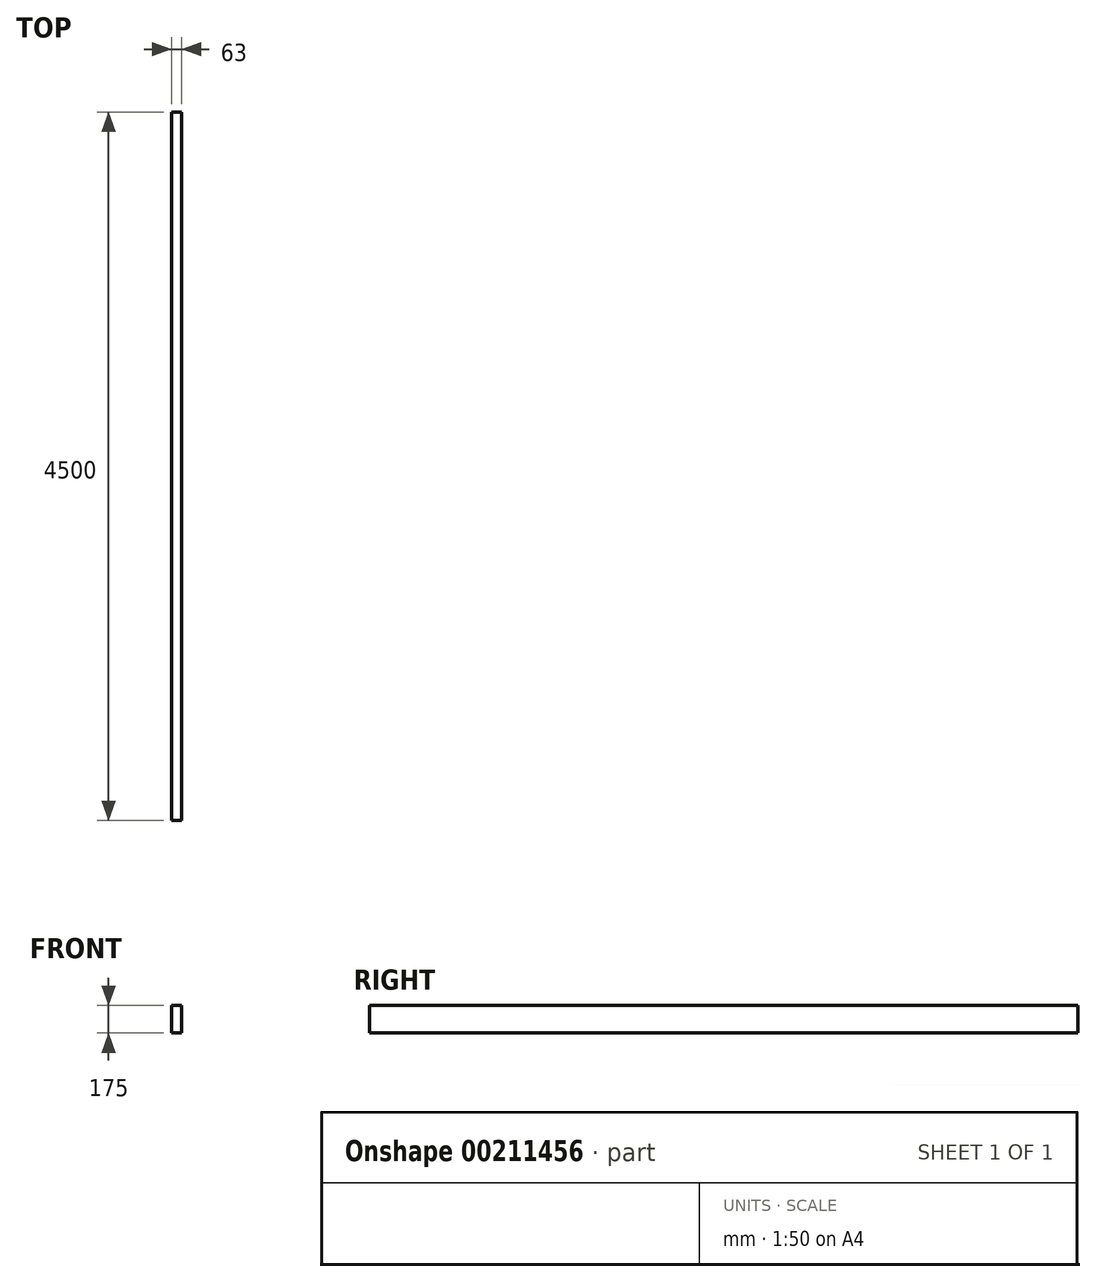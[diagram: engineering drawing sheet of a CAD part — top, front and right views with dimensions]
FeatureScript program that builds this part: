
annotation { "Feature Type Name" : "Feature", "Feature Type Description" : "" }
export const myFeature = defineFeature(function(context is Context, id is Id, definition is map)
    precondition{}
    {
        {
            var Q0;
            Q0=qCreatedBy(makeId("Front.planeOp"),FACE);
            var sketch = newSketch(context, id + "F0", { "sketchPlane" : qUnion([Q0])});
            skLineSegment(sketch, "E0.bottom", {"start": v(-28.95, 87.5) * mm, "end": v(34.05, 87.5) * mm});
            skLineSegment(sketch, "E0.top", {"start": v(-28.95, -87.5) * mm, "end": v(34.05, -87.5) * mm});
            skLineSegment(sketch, "E0.left", {"start": v(-28.95, 87.5) * mm, "end": v(-28.95, -87.5) * mm});
            skLineSegment(sketch, "E0.right", {"start": v(34.05, 87.5) * mm, "end": v(34.05, -87.5) * mm});
            skPoint(sketch, "E0.middle", {"position": v(2.55, 0) * mm});
            skSolve(sketch);
        }
        {
            var Q0;
            Q0=qSketchRegion(id+"F0",true);
            extrude(context, id + "F1", {"entities" : qUnion([Q0]), "depth" : 4500 * mm, "symmetric" : true});
        }
    });
